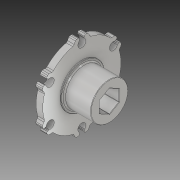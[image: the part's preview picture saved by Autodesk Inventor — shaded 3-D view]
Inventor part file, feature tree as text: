
AUTODESK INVENTOR PART (.ipt)
format: ipt  version: 2018 (Build 220112000, 112)  size: 281,600 bytes
history: native  units: in
note: dims shown in document units (in); Inventor stores cm internally (conversion verified against a paired STEP export)
features: fillet x1
ambient origin geometry x8: Origin, YZ Plane, XZ Plane, XY Plane, X Axis, Y Axis, Z Axis, Center Point
bodies: Solid1 (feature_tree)
feature tree (1):
  fillet  "Fillet7"  [1 undecoded]
note: 1 required parameter value undecoded (feature->parameter linkage not recoverable at this tier; creation-order binding heuristic only, values carry confidence <= 0.55)
